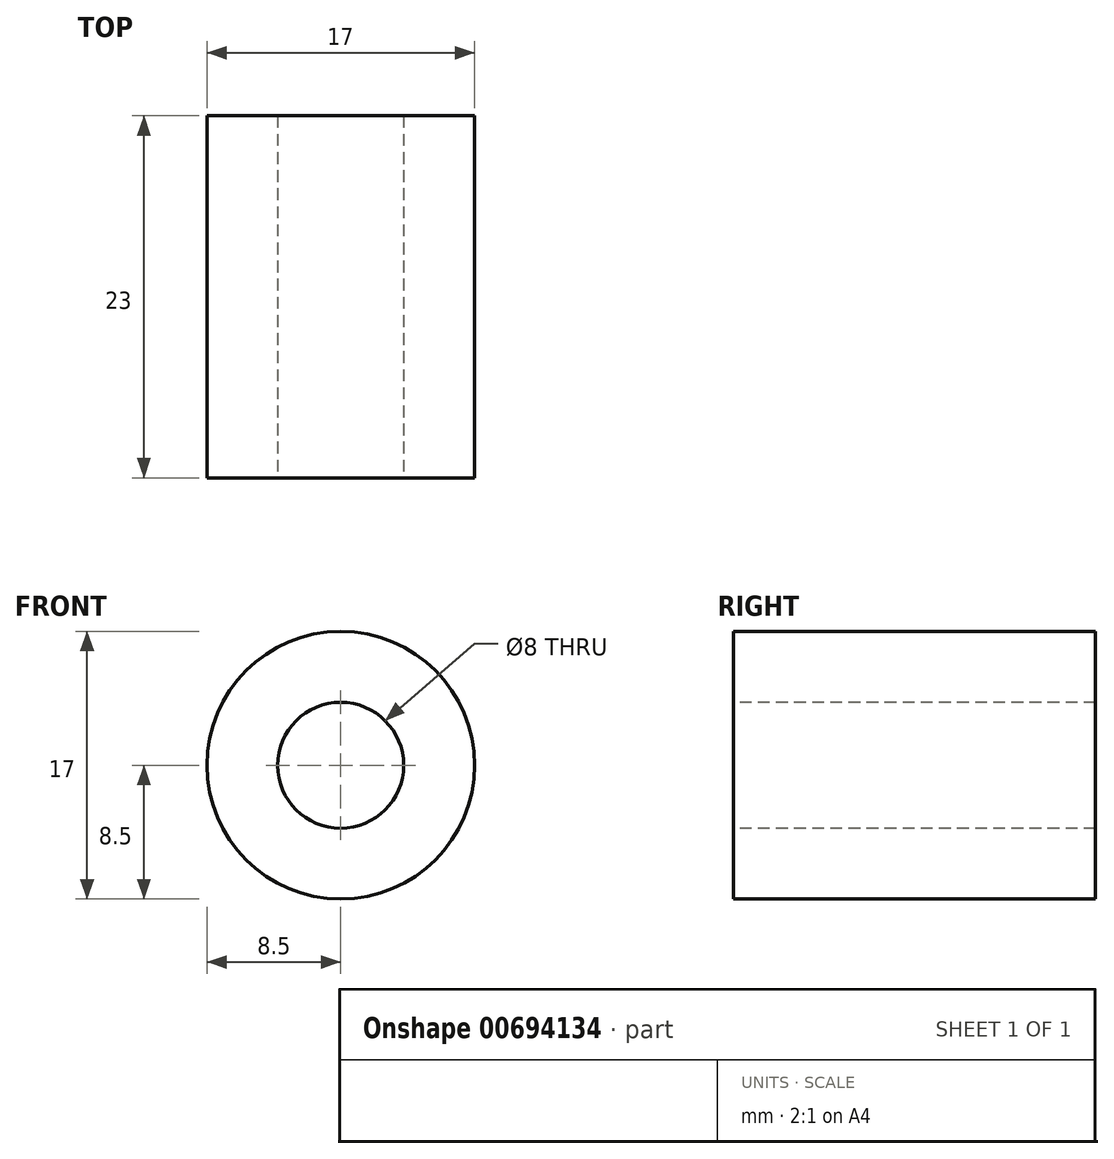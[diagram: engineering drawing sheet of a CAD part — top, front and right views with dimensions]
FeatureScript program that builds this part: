
annotation { "Feature Type Name" : "Feature", "Feature Type Description" : "" }
export const myFeature = defineFeature(function(context is Context, id is Id, definition is map)
    precondition{}
    {
        {
            var Q0;
            Q0=qCreatedBy(makeId("Front.planeOp"),FACE);
            var sketch = newSketch(context, id + "F0", { "sketchPlane" : qUnion([Q0])});
            skCircle(sketch, "E0", {"center": v(0, 0) * mm, "radius": 4 * mm});
            skCircle(sketch, "E1", {"center": v(0, 0) * mm, "radius": 8.5 * mm});
            skSolve(sketch);
        }
        {
            var Q0;
            Q0=makeQuery(id+"F0.imprint","IMPRINT",FACE,{"disambiguationData":[TD([[makeQuery(id+"F0.imprint","IMPRINT",EDGE,{"derivedFrom":sQuery(id+"F0.wireOp",EDGE,"E0")}),-1.0]])]});
            extrude(context, id + "F1", {"entities" : qUnion([Q0]), "oppositeDirection" : true, "depth" : 23 * mm, "offsetDistance" : 25 * mm});
        }
    });
